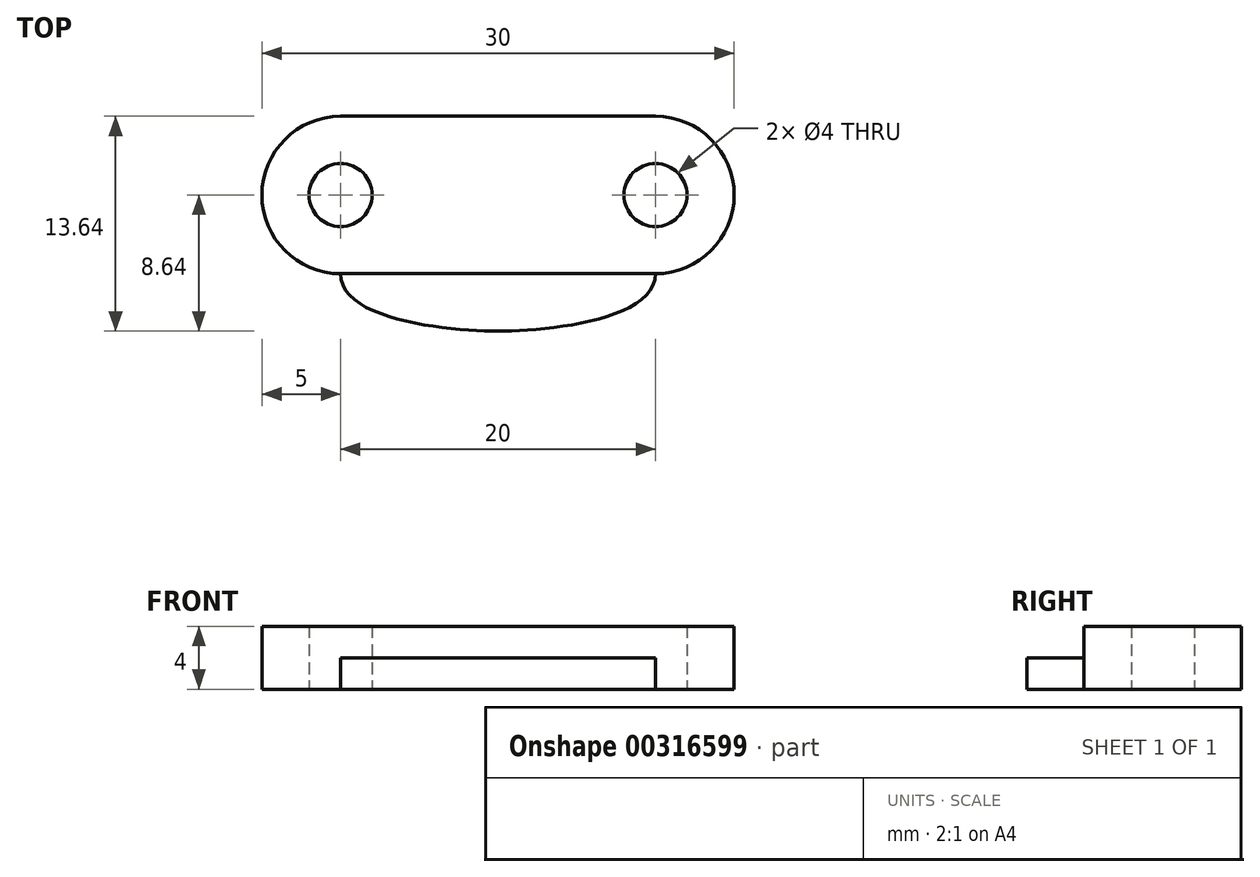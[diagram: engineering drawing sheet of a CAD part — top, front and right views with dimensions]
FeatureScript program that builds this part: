
annotation { "Feature Type Name" : "Feature", "Feature Type Description" : "" }
export const myFeature = defineFeature(function(context is Context, id is Id, definition is map)
    precondition{}
    {
        {
            var Q0;
            Q0=qCreatedBy(makeId("Top.planeOp"),FACE);
            var sketch = newSketch(context, id + "F0", { "sketchPlane" : qUnion([Q0])});
            skLineSegment(sketch, "E0", {"start": v(0, 10) * mm, "end": v(-10, 10) * mm});
            skLineSegment(sketch, "E1", {"start": v(-10, 10) * mm, "end": v(-10, 0) * mm, "construction": true});
            skArc(sketch, "E2", {"start": v(-10, 10) * mm, "mid": v(-15, 5) * mm, "end": v(-10, 0) * mm});
            skLineSegment(sketch, "E3", {"start": v(-10, 0) * mm, "end": v(0, -3.64) * mm, "construction": true});
            skFitSpline(sketch, "E4", {"points": [v(-10, 0) * mm, v(0, -3.64) * mm], "startDerivative": vector(0, -9) * mm, "endDerivative": vector(9, 0) * mm});
            skCircle(sketch, "E5", {"center": v(-10, 5) * mm, "radius": 2 * mm});
            skLineSegment(sketch, "E6", {"start": v(0, 10) * mm, "end": v(0, 0) * mm, "construction": true});
            skLineSegment(sketch, "E7.MirrorCS", {"start": v(0, 10) * mm, "end": v(10, 10) * mm});
            skArc(sketch, "E8.MirrorCS", {"start": v(10, 10) * mm, "mid": v(15, 5) * mm, "end": v(10, 0) * mm});
            skCircle(sketch, "E9.MirrorC", {"center": v(10, 5) * mm, "radius": 2 * mm});
            skFitSpline(sketch, "E10.MirrorCS", {"points": [v(10, 0) * mm, v(0, -3.64) * mm], "startDerivative": vector(0, -9) * mm, "endDerivative": vector(-9, 0) * mm});
            skLineSegment(sketch, "E11", {"start": v(-10, 0) * mm, "end": v(10, 0) * mm});
            skSolve(sketch);
        }
        {
            var Q0;
            Q0=makeQuery(id+"F0.imprint","IMPRINT",FACE,{"disambiguationData":[TD([[makeQuery(id+"F0.imprint","IMPRINT",EDGE,{"derivedFrom":sQuery(id+"F0.wireOp",EDGE,"E4")}),1.0]])]});
            extrude(context, id + "F1", {"entities" : qUnion([Q0]), "depth" : 2 * mm});
        }
        {
            var Q0;
            Q0=makeQuery(id+"F0.imprint","IMPRINT",FACE,{"disambiguationData":[TD([[makeQuery(id+"F0.imprint","IMPRINT",EDGE,{"derivedFrom":sQuery(id+"F0.wireOp",EDGE,"E0")}),1.0]])]});
            extrude(context, id + "F2", {"entities" : qUnion([Q0]), "operationType" : NewBodyOperationType.ADD, "depth" : 4 * mm});
        }
    });
